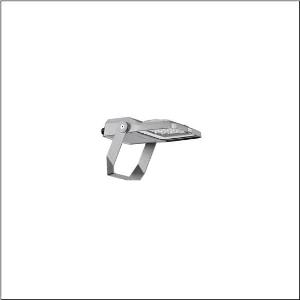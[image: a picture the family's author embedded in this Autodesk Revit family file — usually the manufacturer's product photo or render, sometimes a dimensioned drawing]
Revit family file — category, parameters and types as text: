
# Revit family: floodlight_fl_21_iq_micro___rs12_5xa7761a2b1a_22b8
name_source: partatom
category: Lighting Fixtures
units: mm (PartAtom-declared; Revit-internal decimal feet)

## family parameters
Cut with Voids When Loaded = No
Host = Face
Light Source = No
Part Type = Normal
Room Calculation Point = No
Round Connector Dimension = Use Diameter
Shared = No

## types (1)
- --- (1 x LED, 3090 lm, 23.1 W, 3000K)
    Apparent Load = 23 VA
    CIE Flux Codes = 79 92 99 100 100
    Color Rendering = 70
    Color Temperature = 3000K
    Default Elevation = 1800 mm
    Description = Floodlight FL 21 iQ micro, floodlight, primary light control with lens, of PMMA, primary optical cover: protective disc, of toughened safety glass, transparent, light distribution: RS12, light emission: direct distribution, installation type: surface-mounted, LED, High Power LED, rated luminous flux: 3.090lm, luminous efficacy: 134lm/W, light colour: 730, colour temperature: 3000K, control: optimised constant luminous flux control (CLO 2.0), Desk-Remote (wireless, voltage-free reading and setting of iQ features in the workshop via application-optimized NFC function/RFID function), Light-Fading, Smart-Wire, Night-Set, Lumen-Switch, Temp-Guard, Auto-Match, with terminal, 6-pole, mains connection: 220..240V, AC, 50/60Hz, start of lifetime: 23W, end of service life: 24W, reduction: 11W, luminaire housing, of diecast aluminium, powder-coated, Siteco® metallic grey (DB 702S), corrosivity category C5 mid according to DIN EN ISO 12944, sealing non-destructively replaceable, mounting bracket, of steel, galvanised, powder-coated, Siteco® metallic grey (DB 702S), protection rating (complete): IP66, insulation class (complete): insulation class II (safety insulation), certification: CE, ENEC, VDE, protection symbol: D, impact resistance: IK07, permissible operating ambient temperature: -40..+40°C, permissible operating ambient temperature for outdoor applications: -40..+50°C, standard: DIN EN 12944, LABS conformity tested according to VDMA 24364:2018-05, packaging unit: 1 piece

Light Distribution: RS12
    Height = 65 mm
    Lamp = 1 x LED
    Lamp Light Flux = 3090 lm
    Lamp Power = 23.1 W
    Lamp count = 1
    Length = 312 mm
    Luminous efficacy = 134 lm/W
    Manufacturer = Siteco
    ModVariant = No
    Model = 5XA7761A2B1A
    Mounting Place = Wall
    Mounting Type = Surface mounted
    Number of Poles = 1
    OnlyDefault = Yes
    Power Factor = 1
    Product Name = Floodlight FL 21 iQ micro | RS12
    Product group = floodlight | wall mounted
    ProductGroupID = 2001
    Protection Class = Protection class II
    Protection Degree = IP 66
    RLX_Detail_Level = 1
    RLX_Emergency_Light_Flux = 0 lm
    RLX_Emergency_Type = 0
    RLX_Emergency_Type_DB = No
    RlxData = <blob elided: 74973 chars, md5=f783e526>
    Socket = socket
    Standby Power = 0 W
    System Light Flux = 3090 lm
    System Power = 23 W
    Type Comments = factory setting: luminous flux: 100 % | dim-lin: 254 | 455 mA
    Type Image = l_1006880.jpg
    URL = http://relux.com
    VarID = @adj_133377
    Voltage = 0 V
    Weight = 0.00 kg
    Width = 230 mm

## geometry (parser evidence)
native form markers: Blend x4, Sweep x12
no freeform markers — native parametric forms only
